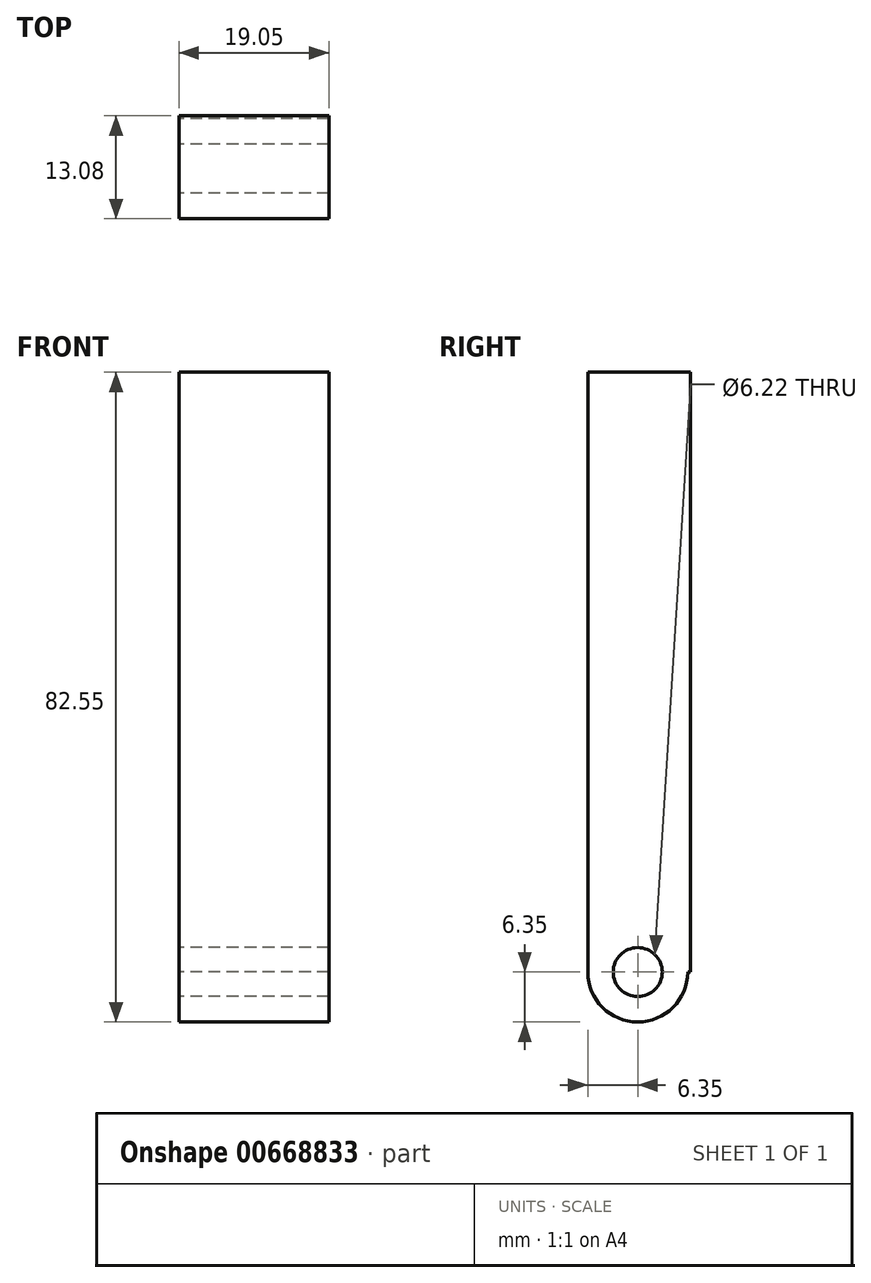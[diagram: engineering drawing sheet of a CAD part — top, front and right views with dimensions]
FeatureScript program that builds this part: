
annotation { "Feature Type Name" : "Feature", "Feature Type Description" : "" }
export const myFeature = defineFeature(function(context is Context, id is Id, definition is map)
    precondition{}
    {
        {
            var Q0;
            Q0=qCreatedBy(makeId("Right.planeOp"),FACE);
            var sketch = newSketch(context, id + "F0", { "sketchPlane" : qUnion([Q0])});
            skCircle(sketch, "E0", {"center": v(0, 0) * mm, "radius": 6.35 * mm});
            skLineSegment(sketch, "E1.bottom", {"start": v(-6.35, 0) * mm, "end": v(6.73, 0) * mm});
            skLineSegment(sketch, "E1.top", {"start": v(-6.35, 76.2) * mm, "end": v(6.73, 76.2) * mm});
            skLineSegment(sketch, "E1.left", {"start": v(-6.35, 0) * mm, "end": v(-6.35, 76.2) * mm});
            skLineSegment(sketch, "E1.right", {"start": v(6.73, 0) * mm, "end": v(6.73, 76.2) * mm});
            skCircle(sketch, "E2", {"center": v(0, 0) * mm, "radius": 3.11 * mm});
            skSolve(sketch);
        }
        {
            var Q0;
            Q0=makeQuery(id+"F0.imprint","IMPRINT",FACE,{"disambiguationData":[TD([[makeQuery(id+"F0.imprint","IMPRINT",EDGE,{"derivedFrom":sQuery(id+"F0.wireOp",EDGE,"E1.top")}),-1.0]])]});
            var Q1;
            {var subQ0=sQuery(id+"F0.wireOp",EDGE,"E1.bottom");var subQ1=sQuery(id+"F0.wireOp",EDGE,"E0");var subQ3=makeQuery(id+"F0.imprint","INTERSECT",VERTEX,{"derivedFrom":[subQ1,subQ0]});Q1=makeQuery(id+"F0.imprint","IMPRINT",FACE,{"disambiguationData":[TD([[makeQuery(id+"F0.imprint","IMPRINT",EDGE,{"disambiguationData":[TD([[subQ3,1.0]])],"derivedFrom":subQ0}),1.0]])]});}
            var Q2;
            {var subQ0=sQuery(id+"F0.wireOp",EDGE,"E1.bottom");var subQ1=sQuery(id+"F0.wireOp",EDGE,"E0");var subQ3=makeQuery(id+"F0.imprint","INTERSECT",VERTEX,{"derivedFrom":[subQ1,subQ0]});Q2=makeQuery(id+"F0.imprint","IMPRINT",FACE,{"disambiguationData":[TD([[makeQuery(id+"F0.imprint","IMPRINT",EDGE,{"disambiguationData":[TD([[subQ3,1.0]])],"derivedFrom":subQ0}),-1.0]])]});}
            extrude(context, id + "F1", {"entities" : qUnion([Q0, Q1, Q2]), "depth" : 19.05 * mm, "offsetDistance" : 25.4 * mm});
        }
    });
